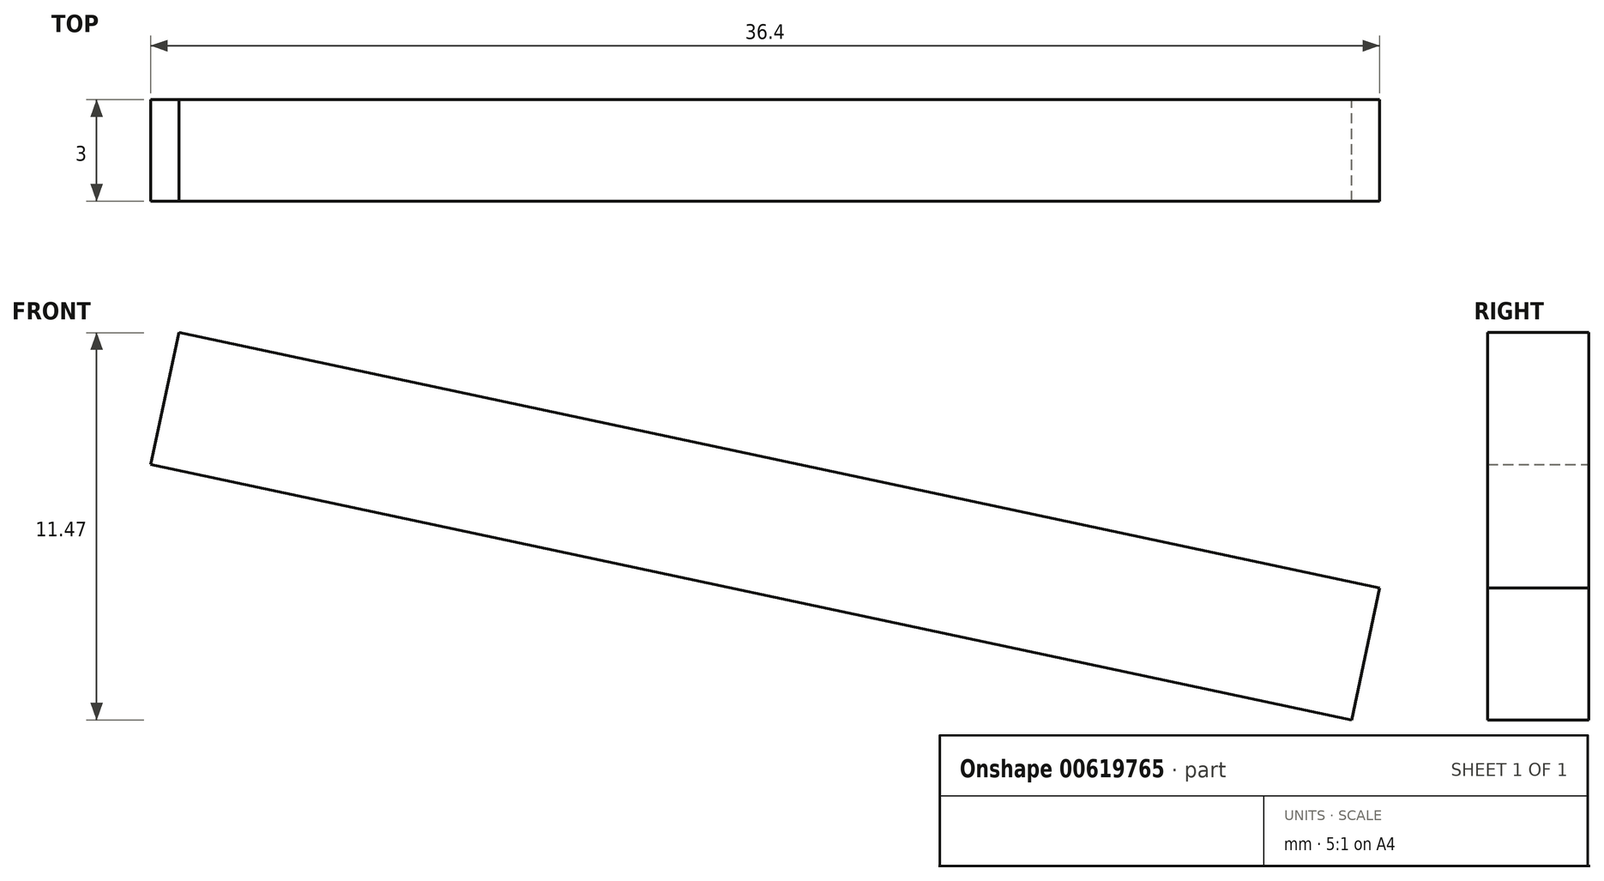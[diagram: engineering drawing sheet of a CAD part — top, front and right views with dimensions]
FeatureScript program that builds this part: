
annotation { "Feature Type Name" : "Feature", "Feature Type Description" : "" }
export const myFeature = defineFeature(function(context is Context, id is Id, definition is map)
    precondition{}
    {
        {
            var Q0;
            Q0=qCreatedBy(makeId("Front.planeOp"),FACE);
            var sketch = newSketch(context, id + "F0", { "sketchPlane" : qUnion([Q0])});
            skLineSegment(sketch, "E0", {"start": v(-59.52, 7.56) * mm, "end": v(-23.95, 0) * mm});
            skLineSegment(sketch, "E1", {"start": v(-23.95, 0) * mm, "end": v(-22.82, 1.8) * mm});
            skLineSegment(sketch, "E2", {"start": v(-22.82, 1.8) * mm, "end": v(-23.12, 3.91) * mm});
            skLineSegment(sketch, "E3", {"start": v(-23.12, 3.91) * mm, "end": v(-58.69, 11.47) * mm});
            skLineSegment(sketch, "E4", {"start": v(-33.2, 4) * mm, "end": v(-10.7, -0.77) * mm, "construction": true});
            skLineSegment(sketch, "E5", {"start": v(0, 0) * mm, "end": v(-40.57, 0) * mm});
            skPoint(sketch, "E6.orphan", {"position": v(-34.94, 4.38) * mm});
            skLineSegment(sketch, "E7", {"start": v(-59.52, 7.56) * mm, "end": v(-58.69, 11.47) * mm});
            skLineSegment(sketch, "E8", {"start": v(-23.95, 0) * mm, "end": v(-23.12, 3.91) * mm});
            skPoint(sketch, "E9", {"position": v(-23.53, 1.96) * mm});
            skSolve(sketch);
        }
        {
            var Q0;
            Q0=makeQuery(id+"F0.imprint","IMPRINT",FACE,{"disambiguationData":[TD([[makeQuery(id+"F0.imprint","IMPRINT",EDGE,{"derivedFrom":sQuery(id+"F0.wireOp",EDGE,"E0")}),1.0]])]});
            extrude(context, id + "F1", {"entities" : qUnion([Q0]), "depth" : 3 * mm, "offsetDistance" : 25 * mm});
        }
    });
